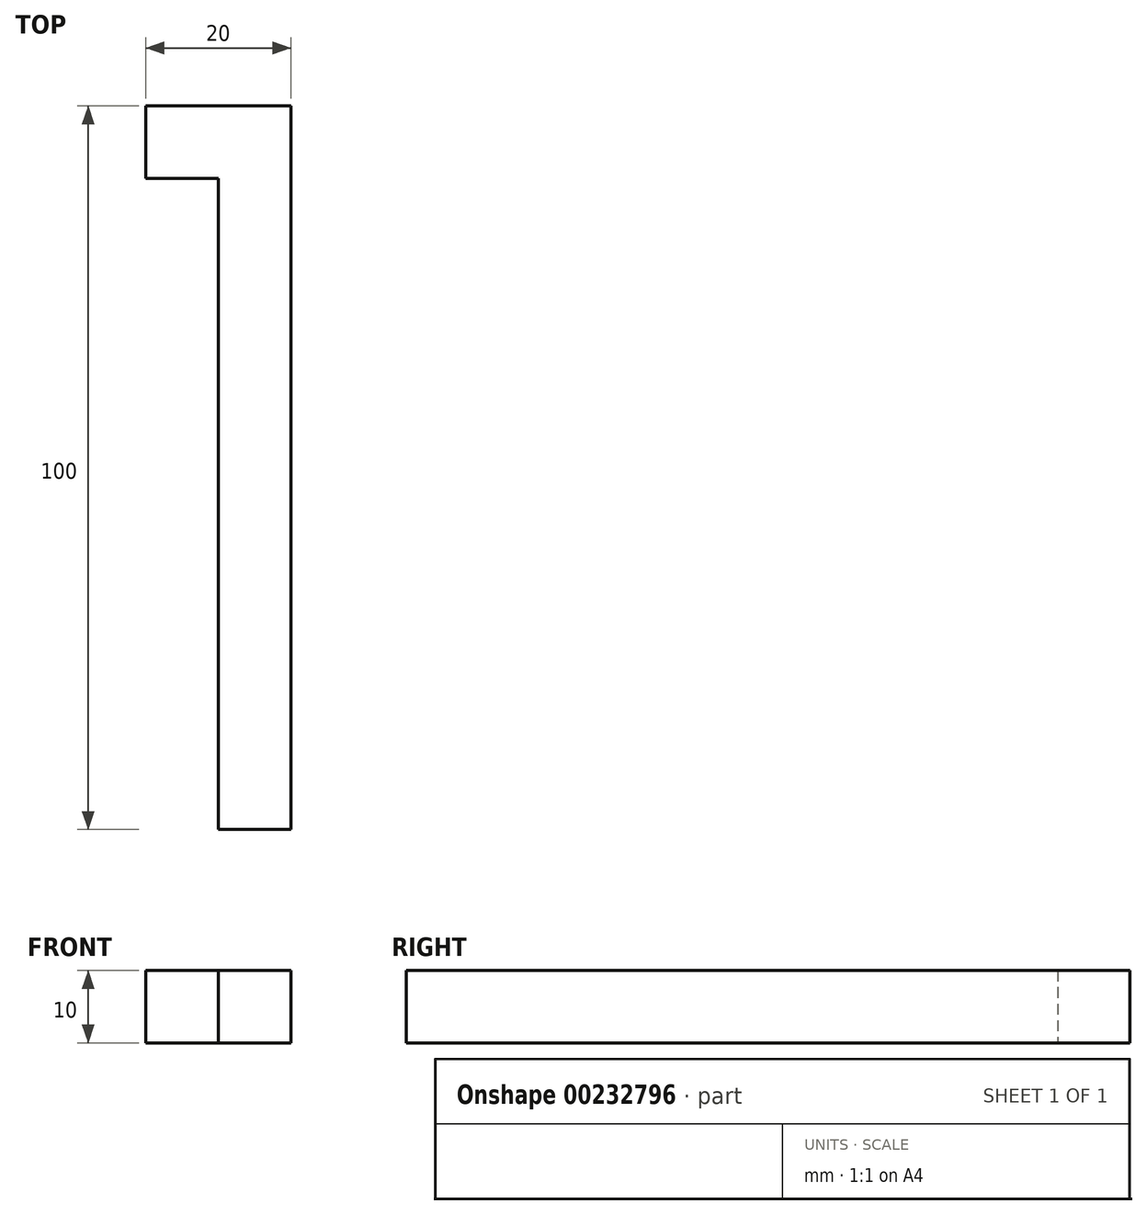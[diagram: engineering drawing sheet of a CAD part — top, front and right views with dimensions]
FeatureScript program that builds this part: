
annotation { "Feature Type Name" : "Feature", "Feature Type Description" : "" }
export const myFeature = defineFeature(function(context is Context, id is Id, definition is map)
    precondition{}
    {
        {
            var Q0;
            Q0=qCreatedBy(makeId("Top.planeOp"),FACE);
            var sketch = newSketch(context, id + "F0", { "sketchPlane" : qUnion([Q0])});
            skLineSegment(sketch, "E0.top", {"start": v(0, -71.64) * mm, "end": v(10, -71.64) * mm});
            skLineSegment(sketch, "E0.left", {"start": v(0, 18.36) * mm, "end": v(0, -71.64) * mm});
            skLineSegment(sketch, "E0.right", {"start": v(10, 28.36) * mm, "end": v(10, -71.64) * mm});
            skLineSegment(sketch, "E1.bottom", {"start": v(-10, 18.36) * mm, "end": v(0, 18.36) * mm});
            skLineSegment(sketch, "E1.top", {"start": v(-10, 28.36) * mm, "end": v(10, 28.36) * mm});
            skLineSegment(sketch, "E1.right", {"start": v(-10, 18.36) * mm, "end": v(-10, 28.36) * mm});
            skPoint(sketch, "E2", {"position": v(0, 18.36) * mm});
            skSolve(sketch);
        }
        {
            var Q0;
            Q0=makeQuery(id+"F0.imprint","IMPRINT",FACE,{"disambiguationData":[TD([[makeQuery(id+"F0.imprint","IMPRINT",EDGE,{"derivedFrom":sQuery(id+"F0.wireOp",EDGE,"E0.top")}),1.0]])]});
            extrude(context, id + "F1", {"entities" : qUnion([Q0]), "depth" : 10 * mm});
        }
    });
